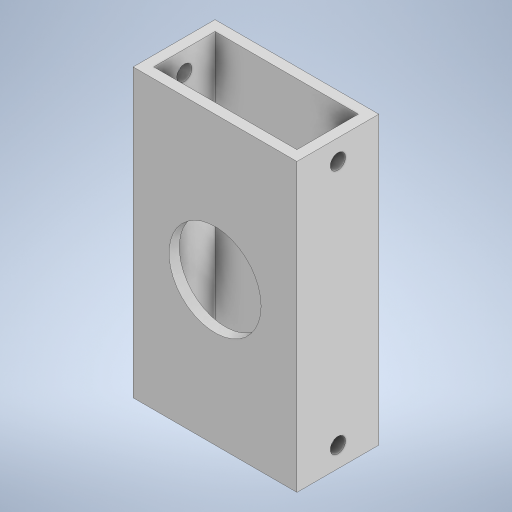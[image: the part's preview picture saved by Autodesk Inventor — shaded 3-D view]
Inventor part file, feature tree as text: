
AUTODESK INVENTOR PART (.ipt)
format: ipt  version: 2023.1 (Build 271208000, 208)  size: 243,712 bytes
history: native  units: in
note: dims shown in document units (in); Inventor stores cm internally (conversion verified against a paired STEP export)
features: extrude x4, sketch x4, projected_geometry x1
ambient origin geometry x8: Origin, YZ Plane, XZ Plane, XY Plane, X Axis, Y Axis, Z Axis, Center Point
bodies: Body1 (feature_tree)
feature tree (9):
  extrude  "Extrusion3"  Depth=1.0in
  extrude  "Extrusion4"  Depth=3.5in TaperAngle=0.0deg
  extrude  "Extrusion5"  Depth=3.5in TaperAngle=0.0deg
  extrude  "Extrusion6"  Depth=1.75in
  sketch  "Sketch3"  dims[d9=2.0in d10=1.0in]
  sketch  "Sketch4"  dims[d11=2.0in d12=3.5in d13=0.0in]
  projected_geometry  "Projected Loop2"
  sketch  "Sketch5"  dims[d14=0.125in d15=3.5in d16=0.0in]
  sketch  "Sketch6"  dims[d17=1.0in d18=1.75in d19=1.125in d20=0.125in d21=0.0in d22=0.5in d23=0.25in d24=0.1875in d26=3.0in d27=0.1875in d28=2.25in d29=0.0in]
